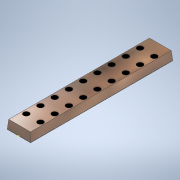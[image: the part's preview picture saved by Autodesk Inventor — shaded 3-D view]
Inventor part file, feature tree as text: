
AUTODESK INVENTOR PART (.ipt)
format: ipt  version: 2021 (Build 250183000, 183)  size: 165,376 bytes
history: native  units: in
note: dims shown in document units (in); Inventor stores cm internally (conversion verified against a paired STEP export)
features: sketch x4, extrude x3, mirror x1, pattern_linear x1, projected_geometry x1
ambient origin geometry x8: Origin, YZ Plane, XZ Plane, XY Plane, X Axis, Y Axis, Z Axis, Center Point
bodies: Solid1 (feature_tree)
feature tree (10):
  sketch  "Sketch1"  dims[d0=0.1614in d1=0.9843in]
  extrude  "Extrusion1"  Depth=0.9843in
  extrude  "Extrusion2"  Depth=0.0709in
  mirror  "Mirror1"
  extrude  "Extrusion3"  Depth=0.0014in
  pattern_linear  "Rectangular Pattern1"  Spacing1=0.0295in  [1 undecoded]
  sketch  "Sketch2"  dims[d2=0.0591in d3=-0.0344in d4=0.0709in]
  sketch  "Sketch3"  dims[d5=0.0014in d6=0.0in d7=0.0394in]
  projected_geometry  "Projected Loop1"
  sketch  "Sketch4"  dims[d8=0.0984in d9=0.0295in d10=0.0in d11=0.0in d12=3.5433in d14=0.0984in d15=0.7874in d17=0.0984in]
note: 1 required parameter value undecoded (feature->parameter linkage not recoverable at this tier; creation-order binding heuristic only, values carry confidence <= 0.55)
